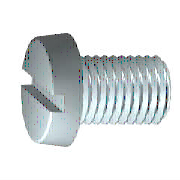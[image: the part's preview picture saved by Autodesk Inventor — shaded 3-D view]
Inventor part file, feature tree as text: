
AUTODESK INVENTOR PART (.ipt)
format: ipt  version: 2023 (Build 270158000, 158)  size: 183,808 bytes
history: native  units: mm (DEFAULTED — no unit token found)
features: sketch x2, extrude x1, plane x1
ambient origin geometry x7: Origin, YZ Plane, XZ Plane, X Axis, Y Axis, Z Axis, Center Point
bodies: Solid1 (feature_tree), Body (feature_tree)
feature tree (4):
  sketch  "Sketch2"  dims[d2=0.49086mm d3=3.3mm d4=5.0mm d5=4.566987mm d8=90.0deg d7=0.0mm d9=8.5mm d10=0.872665mm d11=1.2mm d12=8.5mm d14=0.2mm d15=14.4mm d16=0.0mm d17=0.433015mm d18=0.49086mm d19=1.3mm d20=0.0mm d36=45.0deg d37=0.0mm d39=0.0mm]
  extrude  "Slot"  Depth=14.4mm
  plane  "Work Plane1"
  sketch  "Sketch1"  dims[d0=16.0mm d1=14.4mm]
